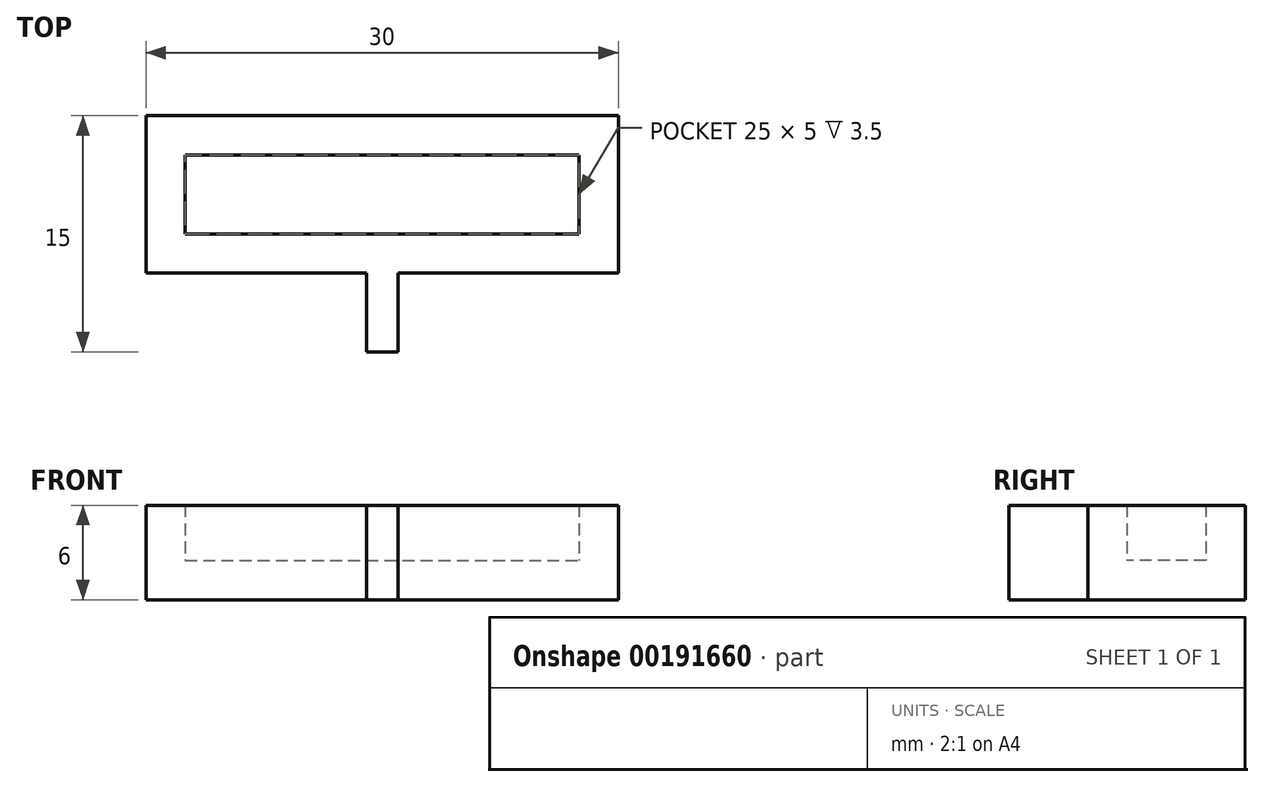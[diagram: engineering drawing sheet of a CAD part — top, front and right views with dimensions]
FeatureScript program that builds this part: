
annotation { "Feature Type Name" : "Feature", "Feature Type Description" : "" }
export const myFeature = defineFeature(function(context is Context, id is Id, definition is map)
    precondition{}
    {
        {
            var Q0;
            Q0=qCreatedBy(makeId("Top.planeOp"),FACE);
            var sketch = newSketch(context, id + "F0", { "sketchPlane" : qUnion([Q0])});
            skLineSegment(sketch, "E0.bottom", {"start": v(0, 0) * mm, "end": v(30, 0) * mm});
            skLineSegment(sketch, "E0.top", {"start": v(0, -10) * mm, "end": v(30, -10) * mm});
            skLineSegment(sketch, "E0.left", {"start": v(0, 0) * mm, "end": v(0, -10) * mm});
            skLineSegment(sketch, "E0.right", {"start": v(30, 0) * mm, "end": v(30, -10) * mm});
            skLineSegment(sketch, "E1.bottom", {"start": v(16, -15) * mm, "end": v(14, -15) * mm});
            skLineSegment(sketch, "E1.top", {"start": v(16, -5) * mm, "end": v(14, -5) * mm});
            skLineSegment(sketch, "E1.left", {"start": v(16, -15) * mm, "end": v(16, -5) * mm});
            skLineSegment(sketch, "E1.right", {"start": v(14, -15) * mm, "end": v(14, -5) * mm});
            skPoint(sketch, "E1.middle", {"position": v(15, -10) * mm});
            skSolve(sketch);
        }
        {
            var Q0;
            Q0=makeQuery(id+"F0.imprint","IMPRINT",FACE,{"disambiguationData":[TD([[makeQuery(id+"F0.imprint","IMPRINT",EDGE,{"derivedFrom":sQuery(id+"F0.wireOp",EDGE,"E0.bottom")}),-1.0]])]});
            var Q1;
            {var subQ5=sQuery(id+"F0.wireOp",EDGE,"E1.top");Q1=makeQuery(id+"F0.imprint","IMPRINT",FACE,{"disambiguationData":[TD([[makeQuery(id+"F0.imprint","IMPRINT",EDGE,{"derivedFrom":subQ5}),1.0]])]});}
            var Q2;
            {var subQ5=sQuery(id+"F0.wireOp",EDGE,"E1.bottom");Q2=makeQuery(id+"F0.imprint","IMPRINT",FACE,{"disambiguationData":[TD([[makeQuery(id+"F0.imprint","IMPRINT",EDGE,{"derivedFrom":subQ5}),-1.0]])]});}
            extrude(context, id + "F1", {"entities" : qUnion([Q0, Q1, Q2]), "depth" : 6 * mm});
        }
        {
            var Q0;
            Q0=makeQuery(id+"F1.opExtrude","CAP_FACE",FACE,{"disambiguationData":[OSD([sQuery(id+"F0.wireOp",EDGE,"E0.bottom"),sQuery(id+"F0.wireOp",EDGE,"E0.top"),sQuery(id+"F0.wireOp",EDGE,"E0.left"),sQuery(id+"F0.wireOp",EDGE,"E0.right"),sQuery(id+"F0.wireOp",EDGE,"E1.bottom"),sQuery(id+"F0.wireOp",EDGE,"E1.left"),sQuery(id+"F0.wireOp",EDGE,"E1.right")])],"isStart":false});
            shell(context, id + "F2", {"entities" : qUnion([Q0]), "thickness" : 2.5 * mm});
        }
    });
